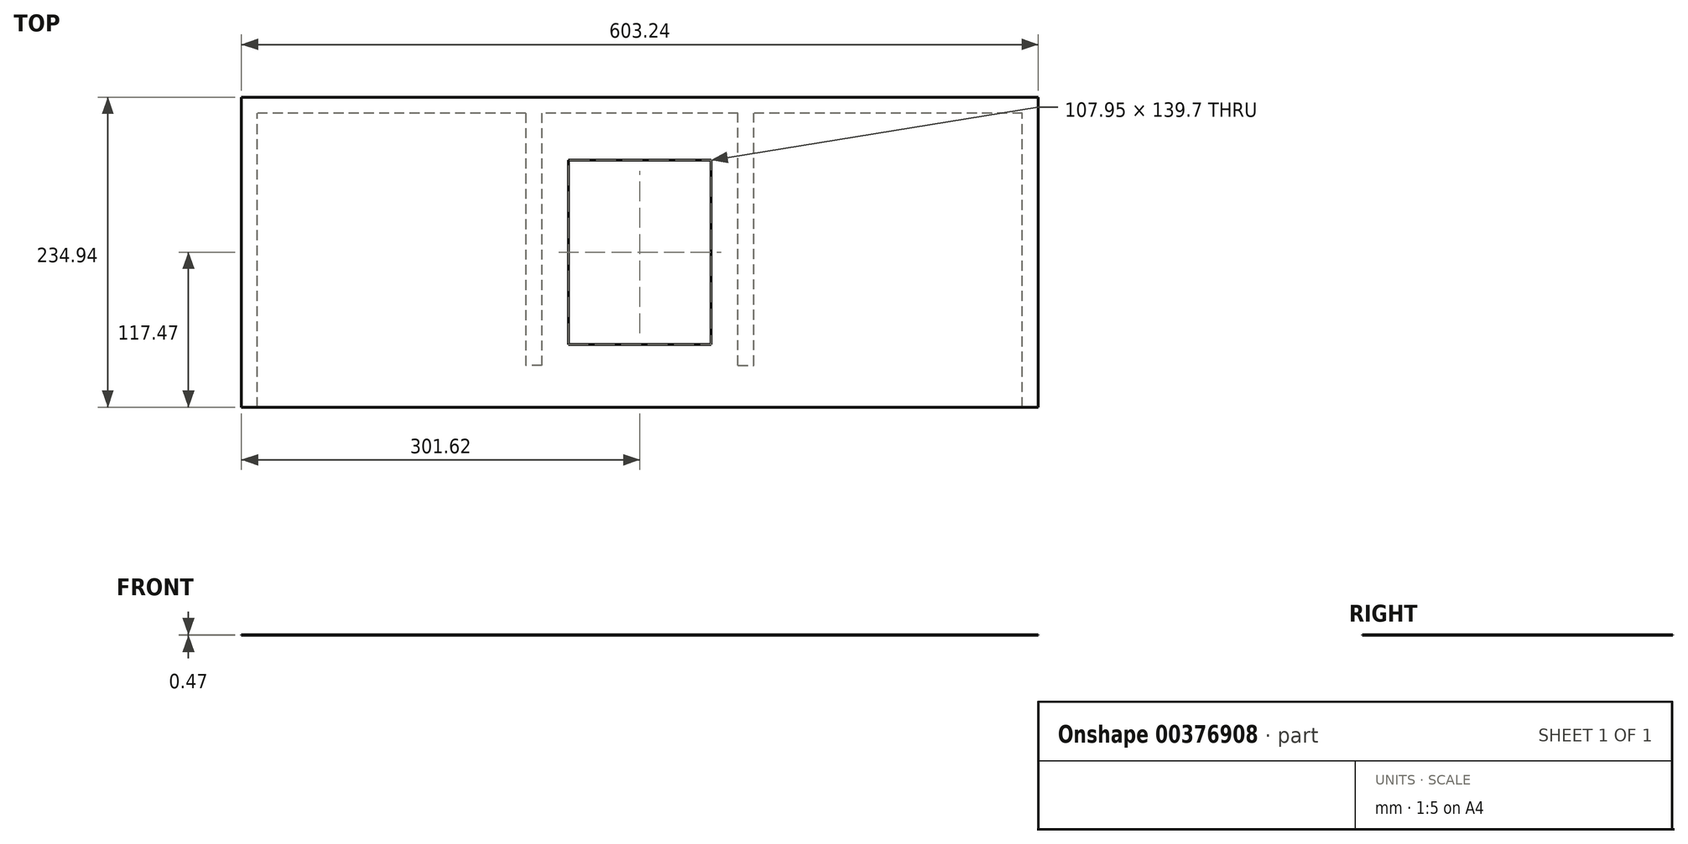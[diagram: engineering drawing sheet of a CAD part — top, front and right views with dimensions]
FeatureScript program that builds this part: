
annotation { "Feature Type Name" : "Feature", "Feature Type Description" : "" }
export const myFeature = defineFeature(function(context is Context, id is Id, definition is map)
    precondition{}
    {
        {
            assignVariable(context, id + "F0", {"name" : "material", "anyValue" : 0.47});
        }
        {
            var Q0;
            Q0=qCreatedBy(makeId("Top.planeOp"),FACE);
            var sketch = newSketch(context, id + "F1", { "sketchPlane" : qUnion([Q0])});
            skLineSegment(sketch, "E0.bottom", {"start": v(301.63, 117.48) * mm, "end": v(-301.63, 117.48) * mm});
            skLineSegment(sketch, "E0.top", {"start": v(301.63, -117.48) * mm, "end": v(-301.63, -117.48) * mm});
            skLineSegment(sketch, "E0.left", {"start": v(301.63, 117.48) * mm, "end": v(301.63, -117.48) * mm});
            skLineSegment(sketch, "E0.right", {"start": v(-301.63, 117.48) * mm, "end": v(-301.63, -117.48) * mm});
            skPoint(sketch, "E0.middle", {"position": v(0, 0) * mm});
            skSolve(sketch);
        }
        {
            var Q0;
            Q0=makeQuery(id+"F1.imprint","IMPRINT",FACE,{"disambiguationData":[TD([[makeQuery(id+"F1.imprint","IMPRINT",EDGE,{"derivedFrom":sQuery(id+"F1.wireOp",EDGE,"E0.bottom")}),1.0]])]});
            extrude(context, id + "F2", {"entities" : qUnion([Q0]), "depth" : (getVariable(context, 'material')) * mm});
        }
        {
            var Q0;
            Q0=makeQuery(id+"F2.opExtrude","CAP_FACE",FACE,{"disambiguationData":[OSD([sQuery(id+"F1.wireOp",EDGE,"E0.bottom"),sQuery(id+"F1.wireOp",EDGE,"E0.top"),sQuery(id+"F1.wireOp",EDGE,"E0.left"),sQuery(id+"F1.wireOp",EDGE,"E0.right")])],"isStart":true});
            var sketch = newSketch(context, id + "F3", { "sketchPlane" : qUnion([Q0])});
            skLineSegment(sketch, "E1.bottom", {"start": v(-301.63, 117.48) * mm, "end": v(-289.56, 117.48) * mm});
            skLineSegment(sketch, "E1.top", {"start": v(-301.63, -117.48) * mm, "end": v(-289.56, -117.48) * mm});
            skLineSegment(sketch, "E1.left", {"start": v(-301.63, 117.48) * mm, "end": v(-301.63, -117.48) * mm});
            skLineSegment(sketch, "E1.right", {"start": v(-289.56, 117.48) * mm, "end": v(-289.56, -117.48) * mm});
            skSolve(sketch);
        }
        {
            var Q0;
            Q0=makeQuery(id+"F3.imprint","IMPRINT",FACE,{"disambiguationData":[TD([[makeQuery(id+"F3.imprint","IMPRINT",EDGE,{"derivedFrom":sQuery(id+"F3.wireOp",EDGE,"E1.bottom")}),1.0]])]});
            extrude(context, id + "F4", {"entities" : qUnion([Q0]), "operationType" : NewBodyOperationType.REMOVE, "oppositeDirection" : true, "depth" : (getVariable(context, 'material') / 2) * mm});
        }
        {
            var Q0;
            Q0=makeQuery(id+"F2.opExtrude","CAP_FACE",FACE,{"disambiguationData":[OSD([sQuery(id+"F1.wireOp",EDGE,"E0.bottom"),sQuery(id+"F1.wireOp",EDGE,"E0.top"),sQuery(id+"F1.wireOp",EDGE,"E0.left"),sQuery(id+"F1.wireOp",EDGE,"E0.right")])],"isStart":true});
            var sketch = newSketch(context, id + "F5", { "sketchPlane" : qUnion([Q0])});
            skLineSegment(sketch, "E2.bottom", {"start": v(301.63, 117.48) * mm, "end": v(289.56, 117.48) * mm});
            skLineSegment(sketch, "E2.top", {"start": v(301.63, -117.48) * mm, "end": v(289.56, -117.48) * mm});
            skLineSegment(sketch, "E2.left", {"start": v(301.63, 117.48) * mm, "end": v(301.63, -117.48) * mm});
            skLineSegment(sketch, "E2.right", {"start": v(289.56, 117.48) * mm, "end": v(289.56, -117.48) * mm});
            skSolve(sketch);
        }
        {
            var Q0;
            Q0=qSketchRegion(id+"F5",true);
            extrude(context, id + "F6", {"entities" : qUnion([Q0]), "operationType" : NewBodyOperationType.REMOVE, "oppositeDirection" : true, "depth" : (getVariable(context, 'material') / 2) * mm});
        }
        {
            var Q0;
            Q0=makeQuery(id+"F2.opExtrude","CAP_FACE",FACE,{"disambiguationData":[OSD([sQuery(id+"F1.wireOp",EDGE,"E0.bottom"),sQuery(id+"F1.wireOp",EDGE,"E0.top"),sQuery(id+"F1.wireOp",EDGE,"E0.left"),sQuery(id+"F1.wireOp",EDGE,"E0.right")])],"isStart":true});
            var sketch = newSketch(context, id + "F7", { "sketchPlane" : qUnion([Q0])});
            skLineSegment(sketch, "E3", {"start": v(289.56, 117.48) * mm, "end": v(86.36, 117.48) * mm, "construction": true});
            skLineSegment(sketch, "E4.bottom", {"start": v(86.36, 117.48) * mm, "end": v(74.3, 117.48) * mm});
            skLineSegment(sketch, "E4.top", {"start": v(86.36, -117.48) * mm, "end": v(74.3, -117.48) * mm});
            skLineSegment(sketch, "E4.left", {"start": v(86.36, 117.48) * mm, "end": v(86.36, -117.48) * mm});
            skLineSegment(sketch, "E4.right", {"start": v(74.3, 117.48) * mm, "end": v(74.3, -117.48) * mm});
            skSolve(sketch);
        }
        {
            var Q0;
            Q0=qSketchRegion(id+"F7",true);
            extrude(context, id + "F8", {"entities" : qUnion([Q0]), "operationType" : NewBodyOperationType.REMOVE, "oppositeDirection" : true, "depth" : (getVariable(context, 'material') / 2) * mm});
        }
        {
            var Q0;
            {var subQ0=sQuery(id+"F1.wireOp",EDGE,"E0.bottom");var subQ1=sQuery(id+"F1.wireOp",EDGE,"E0.top");Q0=makeQuery(id+"F8.boolean.opBoolean","SPLIT",FACE,{"disambiguationData":[TD([makeQuery(id+"F4.boolean.opBoolean","COPY",FACE,{"derivedFrom":makeQuery(id+"F4.opExtrude","SWEPT_FACE",FACE,{"disambiguationData":[OSD([sQuery(id+"F3.wireOp",EDGE,"E1.right")])]})})])],"derivedFrom":makeQuery(id+"F2.opExtrude","CAP_FACE",FACE,{"disambiguationData":[OSD([subQ0,subQ1,sQuery(id+"F1.wireOp",EDGE,"E0.left"),sQuery(id+"F1.wireOp",EDGE,"E0.right")])],"isStart":true})});}
            var sketch = newSketch(context, id + "F9", { "sketchPlane" : qUnion([Q0])});
            skLineSegment(sketch, "E5", {"start": v(-289.56, -117.48) * mm, "end": v(-86.36, -117.48) * mm, "construction": true});
            skLineSegment(sketch, "E6.bottom", {"start": v(-86.36, -117.48) * mm, "end": v(-74.3, -117.48) * mm});
            skLineSegment(sketch, "E6.top", {"start": v(-86.36, 117.48) * mm, "end": v(-74.3, 117.48) * mm});
            skLineSegment(sketch, "E6.left", {"start": v(-86.36, -117.48) * mm, "end": v(-86.36, 117.48) * mm});
            skLineSegment(sketch, "E6.right", {"start": v(-74.3, -117.48) * mm, "end": v(-74.3, 117.48) * mm});
            skSolve(sketch);
        }
        {
            var Q0;
            Q0=makeQuery(id+"F9.imprint","IMPRINT",FACE,{"disambiguationData":[TD([[makeQuery(id+"F9.imprint","IMPRINT",EDGE,{"derivedFrom":sQuery(id+"F9.wireOp",EDGE,"E6.bottom")}),-1.0]])]});
            extrude(context, id + "F10", {"entities" : qUnion([Q0]), "operationType" : NewBodyOperationType.REMOVE, "oppositeDirection" : true, "depth" : (getVariable(context, 'material') / 2) * mm});
        }
        {
            var Q0;
            {var subQ0=sQuery(id+"F1.wireOp",EDGE,"E0.bottom");var subQ1=sQuery(id+"F1.wireOp",EDGE,"E0.top");Q0=makeQuery(id+"F8.boolean.opBoolean","SPLIT",FACE,{"disambiguationData":[TD([makeQuery(id+"F6.boolean.opBoolean","COPY",FACE,{"derivedFrom":makeQuery(id+"F6.opExtrude","SWEPT_FACE",FACE,{"disambiguationData":[OSD([sQuery(id+"F5.wireOp",EDGE,"E2.right")])]})})])],"derivedFrom":makeQuery(id+"F2.opExtrude","CAP_FACE",FACE,{"disambiguationData":[OSD([subQ0,subQ1,sQuery(id+"F1.wireOp",EDGE,"E0.left"),sQuery(id+"F1.wireOp",EDGE,"E0.right")])],"isStart":true})});}
            var sketch = newSketch(context, id + "F11", { "sketchPlane" : qUnion([Q0])});
            skLineSegment(sketch, "E7.bottom", {"start": v(289.56, -117.48) * mm, "end": v(86.36, -117.48) * mm});
            skLineSegment(sketch, "E7.top", {"start": v(289.56, -105.41) * mm, "end": v(86.36, -105.41) * mm});
            skLineSegment(sketch, "E7.left", {"start": v(289.56, -117.48) * mm, "end": v(289.56, -105.41) * mm});
            skLineSegment(sketch, "E7.right", {"start": v(86.36, -117.48) * mm, "end": v(86.36, -105.41) * mm});
            skSolve(sketch);
        }
        {
            var Q0;
            {var subQ0=sQuery(id+"F1.wireOp",EDGE,"E0.bottom");var subQ2=sQuery(id+"F1.wireOp",EDGE,"E0.top");var subQ4=makeQuery(id+"F8.opExtrude","SWEPT_FACE",FACE,{"disambiguationData":[OSD([sQuery(id+"F7.wireOp",EDGE,"E4.right")])]});Q0=makeQuery(id+"F10.boolean.opBoolean","SPLIT",FACE,{"disambiguationData":[TD([makeQuery(id+"F8.boolean.opBoolean","COPY",FACE,{"derivedFrom":subQ4})])],"derivedFrom":makeQuery(id+"F8.boolean.opBoolean","SPLIT",FACE,{"disambiguationData":[TD([makeQuery(id+"F4.boolean.opBoolean","COPY",FACE,{"derivedFrom":makeQuery(id+"F4.opExtrude","SWEPT_FACE",FACE,{"disambiguationData":[OSD([sQuery(id+"F3.wireOp",EDGE,"E1.right")])]})})])],"derivedFrom":makeQuery(id+"F2.opExtrude","CAP_FACE",FACE,{"disambiguationData":[OSD([subQ0,subQ2,sQuery(id+"F1.wireOp",EDGE,"E0.left"),sQuery(id+"F1.wireOp",EDGE,"E0.right")])],"isStart":true})})});}
            var sketch = newSketch(context, id + "F12", { "sketchPlane" : qUnion([Q0])});
            skLineSegment(sketch, "E8.bottom", {"start": v(74.3, -117.48) * mm, "end": v(-74.3, -117.48) * mm});
            skLineSegment(sketch, "E8.top", {"start": v(74.3, -105.41) * mm, "end": v(-74.3, -105.41) * mm});
            skLineSegment(sketch, "E8.left", {"start": v(74.3, -117.48) * mm, "end": v(74.3, -105.41) * mm});
            skLineSegment(sketch, "E8.right", {"start": v(-74.3, -117.48) * mm, "end": v(-74.3, -105.41) * mm});
            skSolve(sketch);
        }
        {
            var Q0;
            {var subQ0=sQuery(id+"F1.wireOp",EDGE,"E0.bottom");var subQ2=makeQuery(id+"F4.boolean.opBoolean","COPY",FACE,{"derivedFrom":makeQuery(id+"F4.opExtrude","SWEPT_FACE",FACE,{"disambiguationData":[OSD([sQuery(id+"F3.wireOp",EDGE,"E1.right")])]})});var subQ3=sQuery(id+"F1.wireOp",EDGE,"E0.top");Q0=makeQuery(id+"F10.boolean.opBoolean","SPLIT",FACE,{"disambiguationData":[TD([subQ2])],"derivedFrom":makeQuery(id+"F8.boolean.opBoolean","SPLIT",FACE,{"disambiguationData":[TD([subQ2])],"derivedFrom":makeQuery(id+"F2.opExtrude","CAP_FACE",FACE,{"disambiguationData":[OSD([subQ0,subQ3,sQuery(id+"F1.wireOp",EDGE,"E0.left"),sQuery(id+"F1.wireOp",EDGE,"E0.right")])],"isStart":true})})});}
            var sketch = newSketch(context, id + "F13", { "sketchPlane" : qUnion([Q0])});
            skLineSegment(sketch, "E9.bottom", {"start": v(-86.36, -117.48) * mm, "end": v(-289.56, -117.48) * mm});
            skLineSegment(sketch, "E9.top", {"start": v(-86.36, -105.41) * mm, "end": v(-289.56, -105.41) * mm});
            skLineSegment(sketch, "E9.left", {"start": v(-86.36, -117.48) * mm, "end": v(-86.36, -105.41) * mm});
            skLineSegment(sketch, "E9.right", {"start": v(-289.56, -117.48) * mm, "end": v(-289.56, -105.41) * mm});
            skSolve(sketch);
        }
        {
            var Q0;
            Q0=makeQuery(id+"F11.imprint","IMPRINT",FACE,{"disambiguationData":[TD([[makeQuery(id+"F11.imprint","IMPRINT",EDGE,{"derivedFrom":sQuery(id+"F11.wireOp",EDGE,"E7.bottom")}),-1.0]])]});
            extrude(context, id + "F14", {"entities" : qUnion([Q0]), "operationType" : NewBodyOperationType.REMOVE, "oppositeDirection" : true, "depth" : (getVariable(context, 'material') / 2) * mm});
        }
        {
            var Q0;
            Q0=makeQuery(id+"F12.imprint","IMPRINT",FACE,{"disambiguationData":[TD([[makeQuery(id+"F12.imprint","IMPRINT",EDGE,{"derivedFrom":sQuery(id+"F12.wireOp",EDGE,"E8.bottom")}),-1.0]])]});
            extrude(context, id + "F15", {"entities" : qUnion([Q0]), "operationType" : NewBodyOperationType.REMOVE, "oppositeDirection" : true, "depth" : (getVariable(context, 'material') / 2) * mm});
        }
        {
            var Q0;
            Q0=makeQuery(id+"F13.imprint","IMPRINT",FACE,{"disambiguationData":[TD([[makeQuery(id+"F13.imprint","IMPRINT",EDGE,{"derivedFrom":sQuery(id+"F13.wireOp",EDGE,"E9.bottom")}),-1.0]])]});
            extrude(context, id + "F16", {"entities" : qUnion([Q0]), "operationType" : NewBodyOperationType.REMOVE, "oppositeDirection" : true, "depth" : (getVariable(context, 'material') / 2) * mm});
        }
        {
            var Q0;
            Q0=makeQuery(id+"F16.boolean.opBoolean","MERGE",FACE,{"derivedFrom":[makeQuery(id+"F4.boolean.opBoolean","COPY",FACE,{"derivedFrom":makeQuery(id+"F4.opExtrude","CAP_FACE",FACE,{"disambiguationData":[OSD([sQuery(id+"F3.wireOp",EDGE,"E1.bottom"),sQuery(id+"F3.wireOp",EDGE,"E1.top"),sQuery(id+"F3.wireOp",EDGE,"E1.left"),sQuery(id+"F3.wireOp",EDGE,"E1.right")])],"isStart":false})}),makeQuery(id+"F15.boolean.opBoolean","MERGE",FACE,{"derivedFrom":[makeQuery(id+"F10.boolean.opBoolean","COPY",FACE,{"derivedFrom":makeQuery(id+"F10.opExtrude","CAP_FACE",FACE,{"disambiguationData":[OSD([sQuery(id+"F9.wireOp",EDGE,"E6.bottom"),sQuery(id+"F9.wireOp",EDGE,"E6.top"),sQuery(id+"F9.wireOp",EDGE,"E6.left"),sQuery(id+"F9.wireOp",EDGE,"E6.right")])],"isStart":false})}),makeQuery(id+"F14.boolean.opBoolean","MERGE",FACE,{"derivedFrom":[makeQuery(id+"F6.boolean.opBoolean","COPY",FACE,{"derivedFrom":makeQuery(id+"F6.opExtrude","CAP_FACE",FACE,{"disambiguationData":[OSD([sQuery(id+"F5.wireOp",EDGE,"E2.bottom"),sQuery(id+"F5.wireOp",EDGE,"E2.top"),sQuery(id+"F5.wireOp",EDGE,"E2.left"),sQuery(id+"F5.wireOp",EDGE,"E2.right")])],"isStart":false})}),makeQuery(id+"F8.boolean.opBoolean","COPY",FACE,{"derivedFrom":makeQuery(id+"F8.opExtrude","CAP_FACE",FACE,{"disambiguationData":[OSD([sQuery(id+"F7.wireOp",EDGE,"E4.bottom"),sQuery(id+"F7.wireOp",EDGE,"E4.top"),sQuery(id+"F7.wireOp",EDGE,"E4.left"),sQuery(id+"F7.wireOp",EDGE,"E4.right")])],"isStart":false})}),makeQuery(id+"F14.opExtrude","CAP_FACE",FACE,{"disambiguationData":[OSD([sQuery(id+"F11.wireOp",EDGE,"E7.bottom"),sQuery(id+"F11.wireOp",EDGE,"E7.top"),sQuery(id+"F11.wireOp",EDGE,"E7.left"),sQuery(id+"F11.wireOp",EDGE,"E7.right")])],"isStart":false})]}),makeQuery(id+"F15.opExtrude","CAP_FACE",FACE,{"disambiguationData":[OSD([sQuery(id+"F12.wireOp",EDGE,"E8.bottom"),sQuery(id+"F12.wireOp",EDGE,"E8.top"),sQuery(id+"F12.wireOp",EDGE,"E8.left"),sQuery(id+"F12.wireOp",EDGE,"E8.right")])],"isStart":false})]}),makeQuery(id+"F16.opExtrude","CAP_FACE",FACE,{"disambiguationData":[OSD([sQuery(id+"F13.wireOp",EDGE,"E9.bottom"),sQuery(id+"F13.wireOp",EDGE,"E9.top"),sQuery(id+"F13.wireOp",EDGE,"E9.left"),sQuery(id+"F13.wireOp",EDGE,"E9.right")])],"isStart":false})]});
            var sketch = newSketch(context, id + "F17", { "sketchPlane" : qUnion([Q0])});
            skLineSegment(sketch, "E10.bottom", {"start": v(74.3, 117.48) * mm, "end": v(86.36, 117.48) * mm});
            skLineSegment(sketch, "E10.top", {"start": v(74.3, 85.73) * mm, "end": v(86.36, 85.73) * mm});
            skLineSegment(sketch, "E10.left", {"start": v(74.3, 117.48) * mm, "end": v(74.3, 85.73) * mm});
            skLineSegment(sketch, "E10.right", {"start": v(86.36, 117.48) * mm, "end": v(86.36, 85.73) * mm});
            skSolve(sketch);
        }
        {
            var Q0;
            Q0=qSketchRegion(id+"F17",true);
            extrude(context, id + "F18", {"entities" : qUnion([Q0]), "operationType" : NewBodyOperationType.ADD, "depth" : (getVariable(context, 'material') / 2) * mm});
        }
        {
            var Q0;
            Q0=makeQuery(id+"F16.boolean.opBoolean","MERGE",FACE,{"derivedFrom":[makeQuery(id+"F4.boolean.opBoolean","COPY",FACE,{"derivedFrom":makeQuery(id+"F4.opExtrude","CAP_FACE",FACE,{"disambiguationData":[OSD([sQuery(id+"F3.wireOp",EDGE,"E1.bottom"),sQuery(id+"F3.wireOp",EDGE,"E1.top"),sQuery(id+"F3.wireOp",EDGE,"E1.left"),sQuery(id+"F3.wireOp",EDGE,"E1.right")])],"isStart":false})}),makeQuery(id+"F15.boolean.opBoolean","MERGE",FACE,{"derivedFrom":[makeQuery(id+"F10.boolean.opBoolean","COPY",FACE,{"derivedFrom":makeQuery(id+"F10.opExtrude","CAP_FACE",FACE,{"disambiguationData":[OSD([sQuery(id+"F9.wireOp",EDGE,"E6.bottom"),sQuery(id+"F9.wireOp",EDGE,"E6.top"),sQuery(id+"F9.wireOp",EDGE,"E6.left"),sQuery(id+"F9.wireOp",EDGE,"E6.right")])],"isStart":false})}),makeQuery(id+"F14.boolean.opBoolean","MERGE",FACE,{"derivedFrom":[makeQuery(id+"F6.boolean.opBoolean","COPY",FACE,{"derivedFrom":makeQuery(id+"F6.opExtrude","CAP_FACE",FACE,{"disambiguationData":[OSD([sQuery(id+"F5.wireOp",EDGE,"E2.bottom"),sQuery(id+"F5.wireOp",EDGE,"E2.top"),sQuery(id+"F5.wireOp",EDGE,"E2.left"),sQuery(id+"F5.wireOp",EDGE,"E2.right")])],"isStart":false})}),makeQuery(id+"F8.boolean.opBoolean","COPY",FACE,{"derivedFrom":makeQuery(id+"F8.opExtrude","CAP_FACE",FACE,{"disambiguationData":[OSD([sQuery(id+"F7.wireOp",EDGE,"E4.bottom"),sQuery(id+"F7.wireOp",EDGE,"E4.top"),sQuery(id+"F7.wireOp",EDGE,"E4.left"),sQuery(id+"F7.wireOp",EDGE,"E4.right")])],"isStart":false})}),makeQuery(id+"F14.opExtrude","CAP_FACE",FACE,{"disambiguationData":[OSD([sQuery(id+"F11.wireOp",EDGE,"E7.bottom"),sQuery(id+"F11.wireOp",EDGE,"E7.top"),sQuery(id+"F11.wireOp",EDGE,"E7.left"),sQuery(id+"F11.wireOp",EDGE,"E7.right")])],"isStart":false})]}),makeQuery(id+"F15.opExtrude","CAP_FACE",FACE,{"disambiguationData":[OSD([sQuery(id+"F12.wireOp",EDGE,"E8.bottom"),sQuery(id+"F12.wireOp",EDGE,"E8.top"),sQuery(id+"F12.wireOp",EDGE,"E8.left"),sQuery(id+"F12.wireOp",EDGE,"E8.right")])],"isStart":false})]}),makeQuery(id+"F16.opExtrude","CAP_FACE",FACE,{"disambiguationData":[OSD([sQuery(id+"F13.wireOp",EDGE,"E9.bottom"),sQuery(id+"F13.wireOp",EDGE,"E9.top"),sQuery(id+"F13.wireOp",EDGE,"E9.left"),sQuery(id+"F13.wireOp",EDGE,"E9.right")])],"isStart":false})]});
            var sketch = newSketch(context, id + "F19", { "sketchPlane" : qUnion([Q0])});
            skLineSegment(sketch, "E11.bottom", {"start": v(-74.3, 117.48) * mm, "end": v(-86.36, 117.48) * mm});
            skLineSegment(sketch, "E11.top", {"start": v(-74.3, 85.73) * mm, "end": v(-86.36, 85.73) * mm});
            skLineSegment(sketch, "E11.left", {"start": v(-74.3, 117.48) * mm, "end": v(-74.3, 85.73) * mm});
            skLineSegment(sketch, "E11.right", {"start": v(-86.36, 117.48) * mm, "end": v(-86.36, 85.73) * mm});
            skSolve(sketch);
        }
        {
            var Q0;
            Q0=qSketchRegion(id+"F19",true);
            extrude(context, id + "F20", {"entities" : qUnion([Q0]), "operationType" : NewBodyOperationType.ADD, "depth" : (getVariable(context, 'material') / 2) * mm});
        }
        {
            var Q0;
            Q0=makeQuery(id+"F2.opExtrude","CAP_FACE",FACE,{"disambiguationData":[OSD([sQuery(id+"F1.wireOp",EDGE,"E0.bottom"),sQuery(id+"F1.wireOp",EDGE,"E0.top"),sQuery(id+"F1.wireOp",EDGE,"E0.left"),sQuery(id+"F1.wireOp",EDGE,"E0.right")])],"isStart":false});
            var sketch = newSketch(context, id + "F21", { "sketchPlane" : qUnion([Q0])});
            skLineSegment(sketch, "E12.bottom", {"start": v(-301.63, -117.48) * mm, "end": v(77.9, -117.48) * mm, "construction": true});
            skLineSegment(sketch, "E12.top", {"start": v(-301.63, 0) * mm, "end": v(77.9, 0) * mm, "construction": true});
            skLineSegment(sketch, "E12.left", {"start": v(-301.63, -117.48) * mm, "end": v(-301.63, 0) * mm, "construction": true});
            skLineSegment(sketch, "E12.right", {"start": v(77.9, -117.48) * mm, "end": v(77.9, 0) * mm, "construction": true});
            skLineSegment(sketch, "E13.bottom", {"start": v(0, -117.48) * mm, "end": v(72.6, -117.48) * mm, "construction": true});
            skLineSegment(sketch, "E13.top", {"start": v(0, 87.9) * mm, "end": v(72.6, 87.9) * mm, "construction": true});
            skLineSegment(sketch, "E13.left", {"start": v(0, -117.48) * mm, "end": v(0, 87.9) * mm, "construction": true});
            skLineSegment(sketch, "E13.right", {"start": v(72.6, -117.48) * mm, "end": v(72.6, 87.9) * mm, "construction": true});
            skLineSegment(sketch, "E14.bottom", {"start": v(53.98, -69.85) * mm, "end": v(-53.97, -69.85) * mm});
            skLineSegment(sketch, "E14.top", {"start": v(53.97, 69.85) * mm, "end": v(-53.98, 69.85) * mm});
            skLineSegment(sketch, "E14.left", {"start": v(53.98, -69.85) * mm, "end": v(53.97, 69.85) * mm});
            skLineSegment(sketch, "E14.right", {"start": v(-53.97, -69.85) * mm, "end": v(-53.98, 69.85) * mm});
            skPoint(sketch, "E14.middle", {"position": v(0, 0) * mm});
            skSolve(sketch);
        }
        {
            var Q0;
            Q0 = qSketchRegion(id + "F21", true);
            extrude(context, id + "F22", {"entities" : qUnion([Q0]), "operationType" : NewBodyOperationType.REMOVE, "oppositeDirection" : true, "depth" : (getVariable(context, 'material')) * mm});
        }
    });
